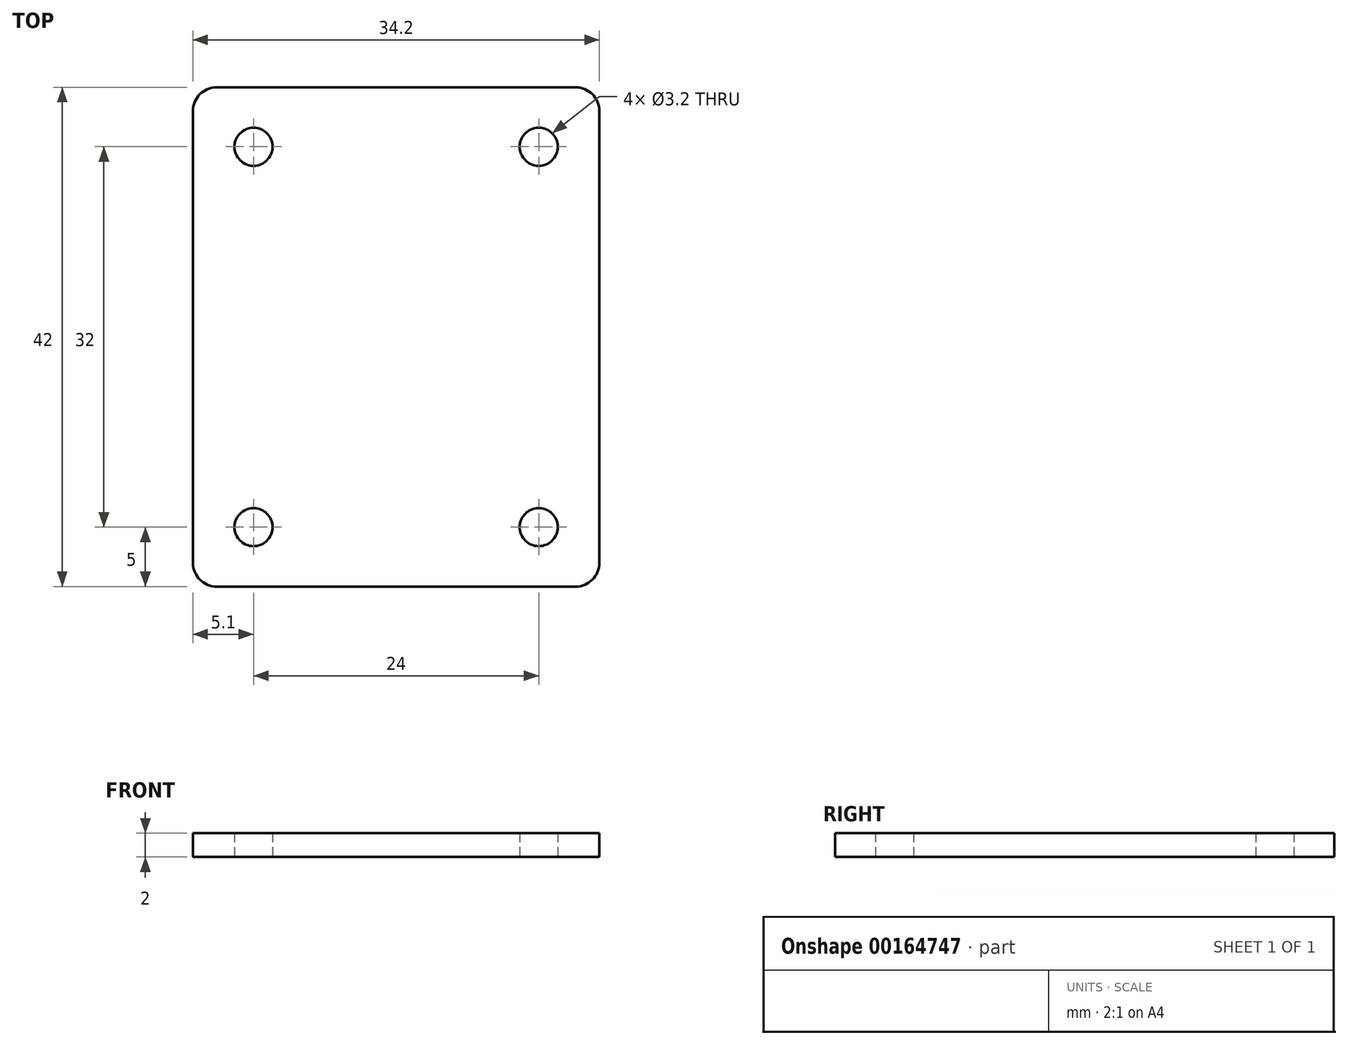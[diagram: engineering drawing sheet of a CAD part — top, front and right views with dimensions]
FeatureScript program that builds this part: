
annotation { "Feature Type Name" : "Feature", "Feature Type Description" : "" }
export const myFeature = defineFeature(function(context is Context, id is Id, definition is map)
    precondition{}
    {
        {
            var Q0;
            Q0=qCreatedBy(makeId("Top.planeOp"),FACE);
            var sketch = newSketch(context, id + "F0", { "sketchPlane" : qUnion([Q0])});
            skLineSegment(sketch, "E0.bottom", {"start": v(-17.1, 21) * mm, "end": v(17.1, 21) * mm});
            skLineSegment(sketch, "E0.top", {"start": v(-17.1, -21) * mm, "end": v(17.1, -21) * mm});
            skLineSegment(sketch, "E0.left", {"start": v(-17.1, 21) * mm, "end": v(-17.1, -21) * mm});
            skLineSegment(sketch, "E0.right", {"start": v(17.1, 21) * mm, "end": v(17.1, -21) * mm});
            skCircle(sketch, "E1", {"center": v(12, -16) * mm, "radius": 1.6 * mm});
            skCircle(sketch, "E2.0.1.0", {"center": v(12, 16) * mm, "radius": 1.6 * mm});
            skCircle(sketch, "E2.1.0.0", {"center": v(-12, -16) * mm, "radius": 1.6 * mm});
            skCircle(sketch, "E2.1.1.0", {"center": v(-12, 16) * mm, "radius": 1.6 * mm});
            skLineSegment(sketch, "E2.direction1", {"start": v(12, -16) * mm, "end": v(-12, -16) * mm, "construction": true});
            skLineSegment(sketch, "E2.direction2", {"start": v(12, -16) * mm, "end": v(12, 16) * mm, "construction": true});
            skSolve(sketch);
        }
        {
            var Q0;
            Q0=makeQuery(id+"F0.imprint","IMPRINT",FACE,{"disambiguationData":[TD([[makeQuery(id+"F0.imprint","IMPRINT",EDGE,{"derivedFrom":sQuery(id+"F0.wireOp",EDGE,"E0.bottom")}),-1.0]])]});
            extrude(context, id + "F1", {"entities" : qUnion([Q0]), "depth" : 2 * mm});
        }
        {
            var Q0;
            Q0=makeQuery(id+"F1.opExtrude","SWEPT_EDGE",EDGE,{"disambiguationData":[OSD([sQuery(id+"F0.wireOp",EDGE,"E0.bottom"),sQuery(id+"F0.wireOp",EDGE,"E0.left")])]});
            var Q1;
            Q1=makeQuery(id+"F1.opExtrude","SWEPT_EDGE",EDGE,{"disambiguationData":[OSD([sQuery(id+"F0.wireOp",EDGE,"E0.top"),sQuery(id+"F0.wireOp",EDGE,"E0.left")])]});
            var Q2;
            Q2=makeQuery(id+"F1.opExtrude","SWEPT_EDGE",EDGE,{"disambiguationData":[OSD([sQuery(id+"F0.wireOp",EDGE,"E0.top"),sQuery(id+"F0.wireOp",EDGE,"E0.right")])]});
            var Q3;
            Q3=makeQuery(id+"F1.opExtrude","SWEPT_EDGE",EDGE,{"disambiguationData":[OSD([sQuery(id+"F0.wireOp",EDGE,"E0.bottom"),sQuery(id+"F0.wireOp",EDGE,"E0.right")])]});
            fillet(context, id + "F2", {"entities" : qUnion([Q0, Q1, Q2, Q3]), "radius" : 2 * mm, "tangentPropagation" : true, "allowEdgeOverflow" : false});
        }
    });
